SOLIDWORKS PART (.sldprt)
format: sldprt  version: not decoded by parser v0  size: 769,024 bytes
history: native  units: mm
features: extrude x7, sketch x4, plane x3, boolean_combine x2, material x1 (+8 scaffold rows collapsed)
feature tree (25):
  scaffold x8  (default folders/planes/origin — collapsed)
  material  "Material <not specified>"
  plane  "Alzado"
  plane  "Planta"
  plane  "Vista lateral"
  sketch  "Croquis1"  dims[D1=0.5mm D2=0.5mm D3=90.0deg D4=2.0mm D5=2.0mm]
  extrude  "Extruir1"  Depth=0mm PW2_UID_val=0mm
  sketch  "Croquis2"  dims[D1=7.5mm D2=0.5mm D3=2.25mm D4=2.0mm]
  extrude  "Extruir2"  [1 undecoded]
  extrude  "pw2 (4)"  Depth=0mm PW2_UID_val=0mm
  sketch  "Croquis3"  dims[c1.D1=0.7mm c1.D2=0.7mm c1.D3=0.9mm c1.D4=0.9mm c1.D5=0.8mm c1.D6=75.0deg c1.D7=0.8mm c1.D8=75.0deg c1.D9=0.8mm c1.D10=15.0deg c1.D11=0.8mm c1.D12=15.0deg c2.D9=~3.285641mm c3.D9=90.0deg c4.D9=0.8mm c4.D10=2.7mm c5.D10=15.0deg c5.D5=0.8mm c5.D7=0.8mm c5.D13=2.0mm c5.D14=2.0mm]
  extrude  "Extruir4"  [1 undecoded]
  extrude  "pw2 (1)"  Depth=0mm PW2_UID_val=0mm
  sketch  "Croquis4"
  extrude  "Extruir5"  [1 undecoded]
  extrude  "pw2 (2)"  Depth=0mm PW2_UID_val=0mm
  boolean_combine  "Combinar1"
  boolean_combine  "Combinar2"
decode coverage: 7 of 13 modeling features carry decoded parameters
note: ~ marks probable driven/reference dimensions
note: 3 parameter values undecoded
summary: no parameter record found for 3 features
note: suppression state not decoded; provenance and decode notes live in map.json
